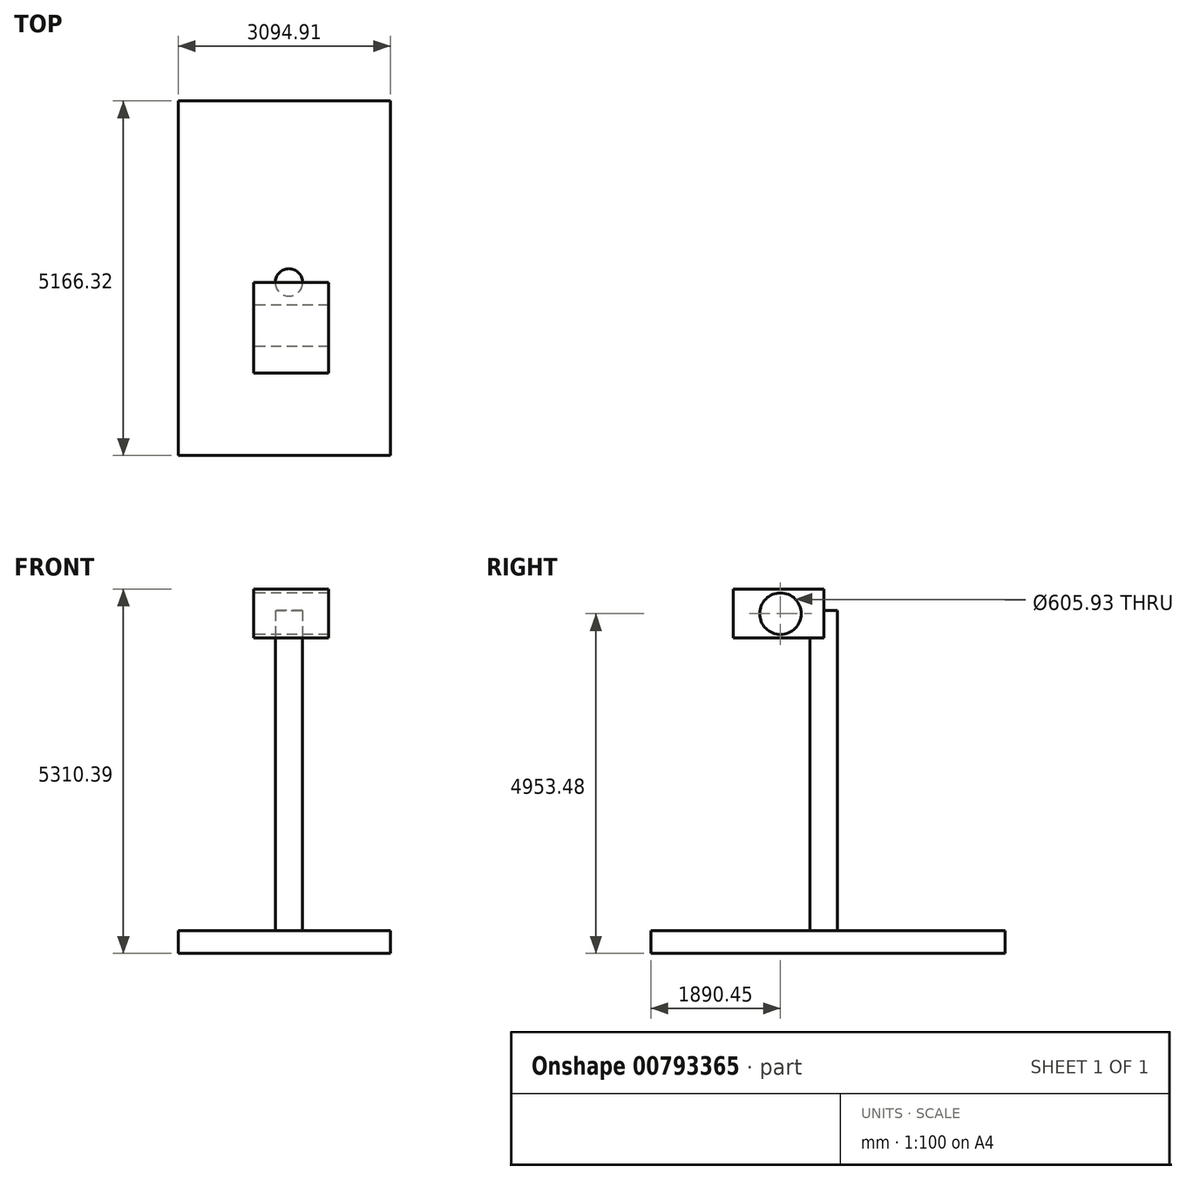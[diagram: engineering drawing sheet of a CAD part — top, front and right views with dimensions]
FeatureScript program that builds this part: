
annotation { "Feature Type Name" : "Feature", "Feature Type Description" : "" }
export const myFeature = defineFeature(function(context is Context, id is Id, definition is map)
    precondition{}
    {
        {
            var Q0;
            Q0=qCreatedBy(makeId("Top.planeOp"),FACE);
            var sketch = newSketch(context, id + "F0", { "sketchPlane" : qUnion([Q0])});
            skCircle(sketch, "E0", {"center": v(0, 0) * mm, "radius": 200 * mm});
            skSolve(sketch);
        }
        {
            var Q0;
            Q0 = qSketchRegion(id + "F0", true);
            extrude(context, id + "F1", {"entities" : qUnion([Q0]), "depth" : 5000 * mm, "offsetDistance" : 25 * mm});
        }
        {
            var Q0;
            Q0=qCreatedBy(makeId("Front.planeOp"),FACE);
            var sketch = newSketch(context, id + "F2", { "sketchPlane" : qUnion([Q0])});
            skLineSegment(sketch, "E1.bottom", {"start": v(-511.35, 5310.39) * mm, "end": v(578.58, 5310.39) * mm});
            skLineSegment(sketch, "E1.top", {"start": v(-511.35, 4599.27) * mm, "end": v(578.58, 4599.27) * mm});
            skLineSegment(sketch, "E1.left", {"start": v(-511.35, 5310.39) * mm, "end": v(-511.35, 4599.27) * mm});
            skLineSegment(sketch, "E1.right", {"start": v(578.58, 5310.39) * mm, "end": v(578.58, 4599.27) * mm});
            skSolve(sketch);
        }
        {
            var Q0;
            Q0 = qSketchRegion(id + "F2", true);
            extrude(context, id + "F3", {"entities" : qUnion([Q0]), "operationType" : NewBodyOperationType.ADD, "depth" : 1320 * mm, "offsetDistance" : 25 * mm});
        }
        {
            var Q0;
            Q0=qCreatedBy(makeId("Top.planeOp"),FACE);
            var sketch = newSketch(context, id + "F4", { "sketchPlane" : qUnion([Q0])});
            skLineSegment(sketch, "E2.bottom", {"start": v(-1612.67, 2644.97) * mm, "end": v(1482.24, 2644.97) * mm});
            skLineSegment(sketch, "E2.top", {"start": v(-1612.67, -2521.35) * mm, "end": v(1482.24, -2521.35) * mm});
            skLineSegment(sketch, "E2.left", {"start": v(-1612.67, 2644.97) * mm, "end": v(-1612.67, -2521.35) * mm});
            skLineSegment(sketch, "E2.right", {"start": v(1482.24, 2644.97) * mm, "end": v(1482.24, -2521.35) * mm});
            skSolve(sketch);
        }
        {
            var Q0;
            Q0 = qSketchRegion(id + "F4", true);
            extrude(context, id + "F5", {"entities" : qUnion([Q0]), "operationType" : NewBodyOperationType.ADD, "depth" : 330 * mm, "offsetDistance" : 25 * mm});
        }
        {
            var Q0;
            Q0=makeQuery(id+"F3.opExtrude","SWEPT_FACE",FACE,{"disambiguationData":[OSD([sQuery(id+"F2.wireOp",EDGE,"E1.left")])]});
            var sketch = newSketch(context, id + "F6", { "sketchPlane" : qUnion([Q0])});
            skCircle(sketch, "E3", {"center": v(630.9, 4953.48) * mm, "radius": 302.97 * mm});
            skSolve(sketch);
        }
        {
            var Q0;
            Q0 = qSketchRegion(id + "F6", true);
            extrude(context, id + "F7", {"entities" : qUnion([Q0]), "operationType" : NewBodyOperationType.REMOVE, "oppositeDirection" : true, "depth" : 1990 * mm, "offsetDistance" : 25 * mm});
        }
    });
